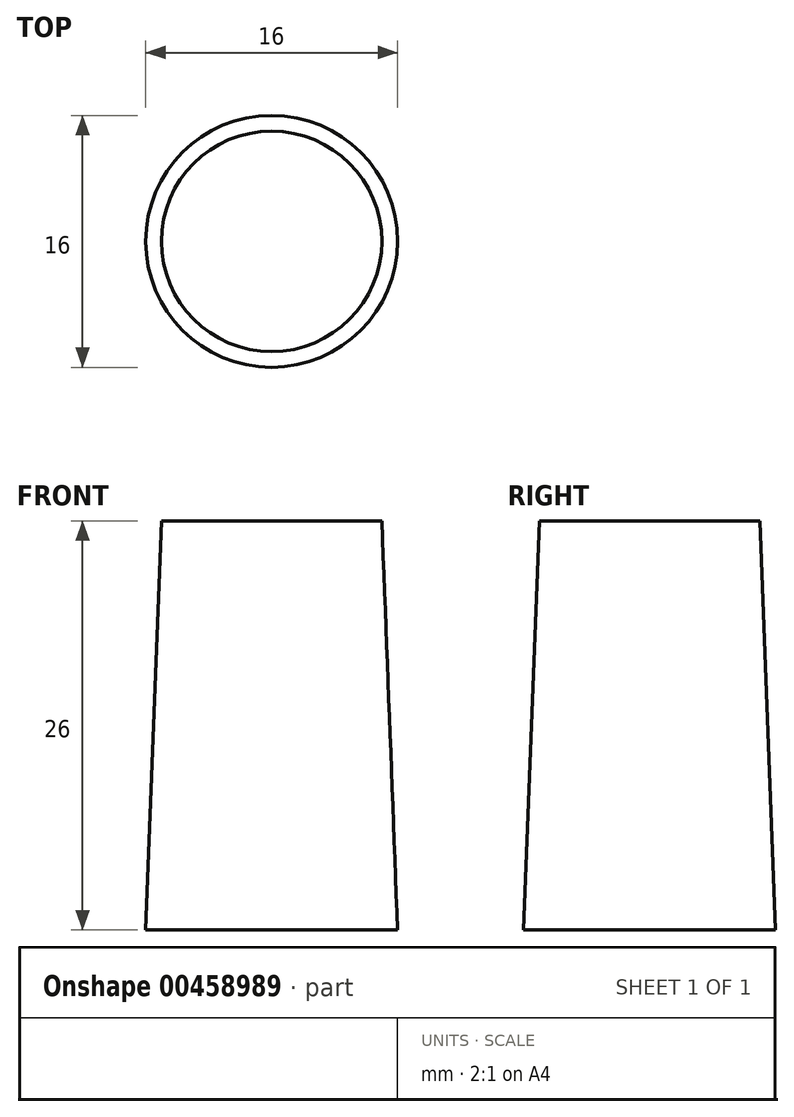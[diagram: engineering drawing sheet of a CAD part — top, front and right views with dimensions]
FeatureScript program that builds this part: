
annotation { "Feature Type Name" : "Feature", "Feature Type Description" : "" }
export const myFeature = defineFeature(function(context is Context, id is Id, definition is map)
    precondition{}
    {
        {
            var Q0;
            Q0=qCreatedBy(makeId("Front.planeOp"),FACE);
            var sketch = newSketch(context, id + "F0", { "sketchPlane" : qUnion([Q0])});
            skLineSegment(sketch, "E0", {"start": v(0, 0) * mm, "end": v(8, 0) * mm});
            skLineSegment(sketch, "E1", {"start": v(8, 0) * mm, "end": v(7, 26) * mm});
            skLineSegment(sketch, "E2", {"start": v(7, 26) * mm, "end": v(0, 26) * mm});
            skLineSegment(sketch, "E3", {"start": v(0, 26) * mm, "end": v(0, 0) * mm});
            skSolve(sketch);
        }
        {
            var Q0;
            Q0 = qSketchRegion(id + "F0", true);
            var Q1;
            Q1=sQuery(id+"F0.wireOp",EDGE,"E3");
            revolve(context, id + "F1", {"entities" : qUnion([Q0]), "axis" : qUnion([Q1]), "revolveType" : RevolveType.FULL});
        }
    });
